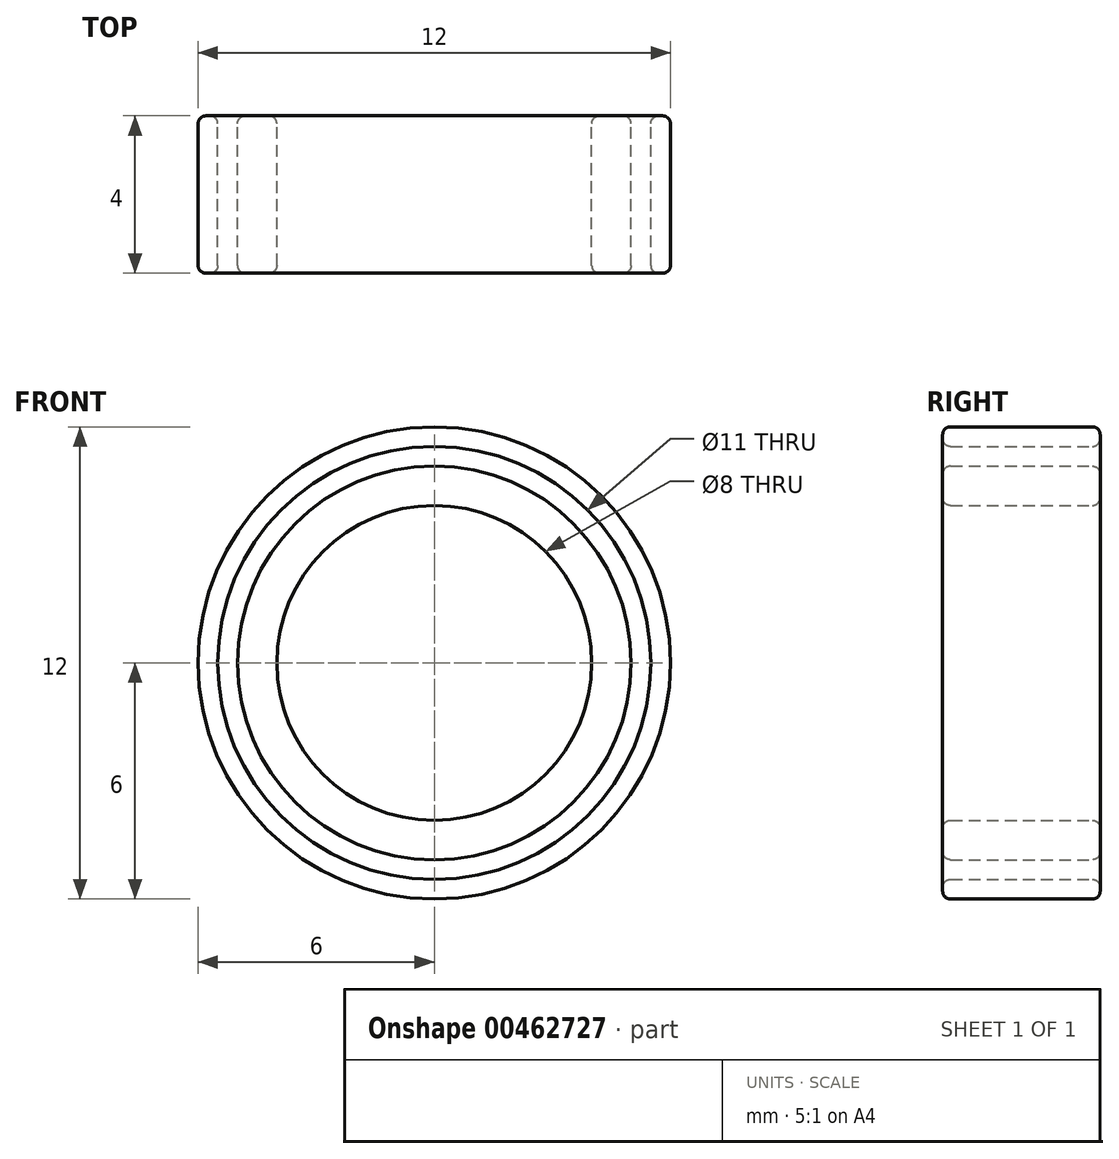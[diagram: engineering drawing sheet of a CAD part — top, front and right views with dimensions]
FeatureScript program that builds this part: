
annotation { "Feature Type Name" : "Feature", "Feature Type Description" : "" }
export const myFeature = defineFeature(function(context is Context, id is Id, definition is map)
    precondition{}
    {
        {
            var Q0;
            Q0=qCreatedBy(makeId("Front.planeOp"),FACE);
            var sketch = newSketch(context, id + "F0", { "sketchPlane" : qUnion([Q0])});
            skCircle(sketch, "E0", {"center": v(0, 0) * mm, "radius": 5.5 * mm});
            skCircle(sketch, "E1", {"center": v(0, 0) * mm, "radius": 6 * mm});
            skCircle(sketch, "E2", {"center": v(0, 0) * mm, "radius": 5 * mm});
            skCircle(sketch, "E3", {"center": v(0, 0) * mm, "radius": 4 * mm});
            skSolve(sketch);
        }
        {
            var Q0;
            Q0 = qSketchRegion(id + "F0", true);
            var Q1;
            Q1=makeQuery(id+"F0.imprint","IMPRINT",FACE,{"disambiguationData":[TD([[makeQuery(id+"F0.imprint","IMPRINT",EDGE,{"derivedFrom":sQuery(id+"F0.wireOp",EDGE,"E2")}),1.0]])]});
            extrude(context, id + "F1", {"entities" : qUnion([Q0, Q1]), "depth" : 4 * mm});
        }
        {
            var Q0;
            Q0=makeQuery(id+"F1.opExtrude","CAP_EDGE",EDGE,{"disambiguationData":[OSD([sQuery(id+"F0.wireOp",EDGE,"E2")])],"isStart":false});
            var Q1;
            Q1=makeQuery(id+"F1.opExtrude","CAP_EDGE",EDGE,{"disambiguationData":[OSD([sQuery(id+"F0.wireOp",EDGE,"E3")])],"isStart":false});
            var Q2;
            Q2=makeQuery(id+"F1.opExtrude","CAP_EDGE",EDGE,{"disambiguationData":[OSD([sQuery(id+"F0.wireOp",EDGE,"E0")])],"isStart":false});
            var Q3;
            Q3=makeQuery(id+"F1.opExtrude","SWEPT_FACE",FACE,{"disambiguationData":[OSD([sQuery(id+"F0.wireOp",EDGE,"E1")])]});
            var Q4;
            Q4=makeQuery(id+"F1.opExtrude","CAP_EDGE",EDGE,{"disambiguationData":[OSD([sQuery(id+"F0.wireOp",EDGE,"E1")])],"isStart":false});
            var Q5;
            Q5=makeQuery(id+"F1.opExtrude","CAP_EDGE",EDGE,{"disambiguationData":[OSD([sQuery(id+"F0.wireOp",EDGE,"E2")])],"isStart":true});
            var Q6;
            Q6=makeQuery(id+"F1.opExtrude","CAP_EDGE",EDGE,{"disambiguationData":[OSD([sQuery(id+"F0.wireOp",EDGE,"E3")])],"isStart":true});
            var Q7;
            Q7=makeQuery(id+"F1.opExtrude","CAP_EDGE",EDGE,{"disambiguationData":[OSD([sQuery(id+"F0.wireOp",EDGE,"E0")])],"isStart":true});
            fillet(context, id + "F2", {"entities" : qUnion([Q0, Q1, Q2, Q3, Q4, Q5, Q6, Q7]), "radius" : 0.2 * mm, "tangentPropagation" : true, "allowEdgeOverflow" : false});
        }
    });
